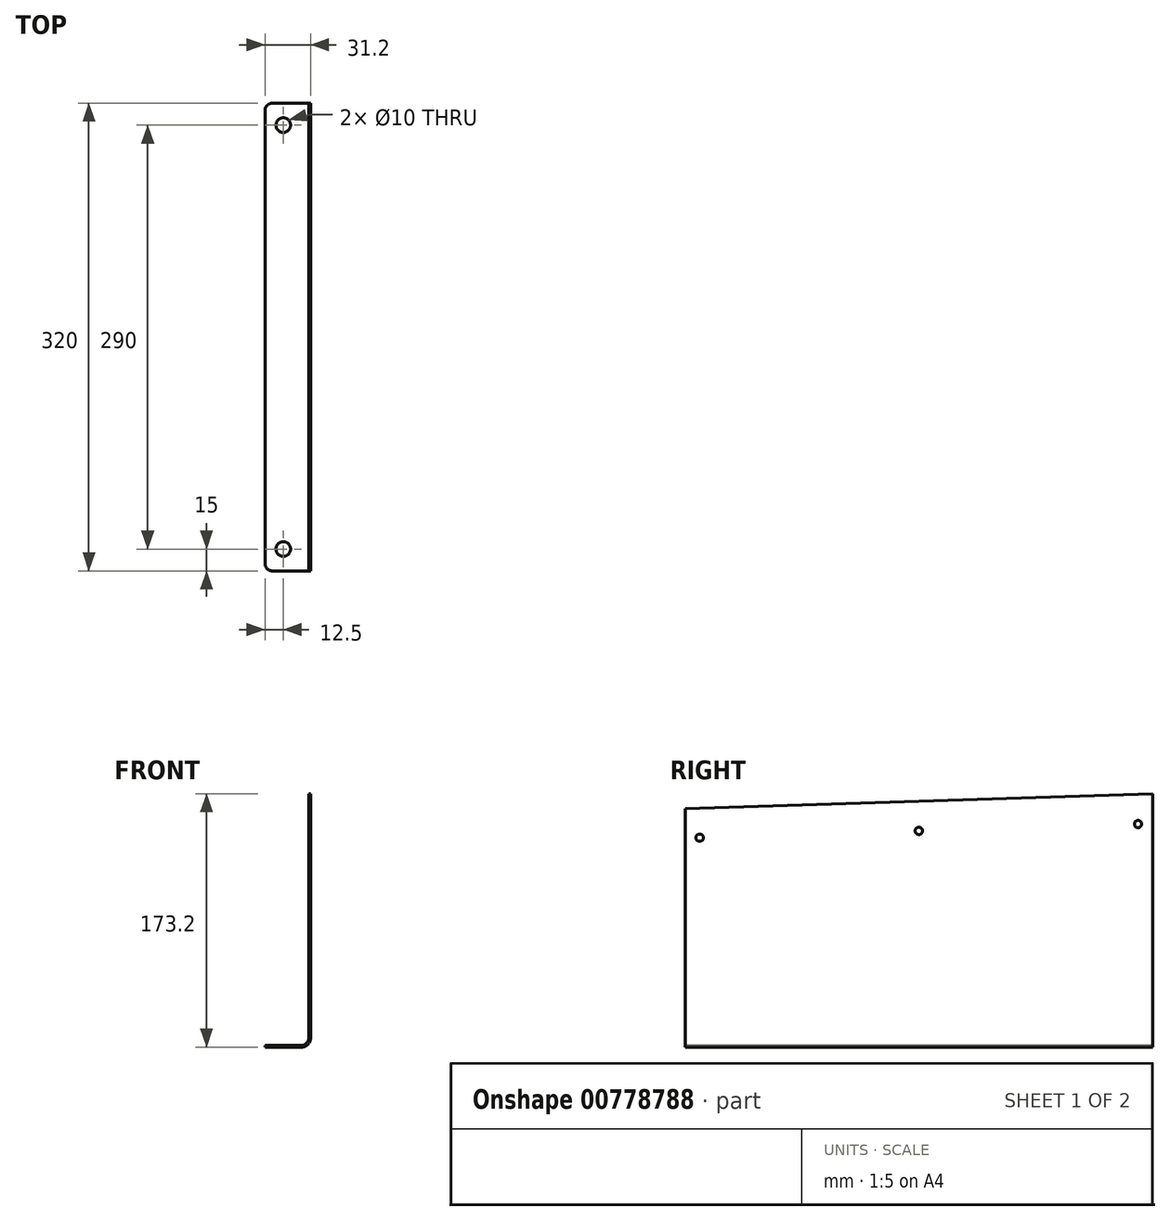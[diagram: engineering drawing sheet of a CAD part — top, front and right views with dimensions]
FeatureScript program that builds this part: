
annotation { "Feature Type Name" : "Feature", "Feature Type Description" : "" }
export const myFeature = defineFeature(function(context is Context, id is Id, definition is map)
    precondition{}
    {
        {
            var Q0;
            Q0=qCreatedBy(makeId("Front.planeOp"),FACE);
            var sketch = newSketch(context, id + "F0", { "sketchPlane" : qUnion([Q0])});
            skLineSegment(sketch, "E0", {"start": v(0, 0) * mm, "end": v(0, -167) * mm});
            skLineSegment(sketch, "E1", {"start": v(-5, -172) * mm, "end": v(-30, -172) * mm});
            skLineSegment(sketch, "E2", {"start": v(-30, -172) * mm, "end": v(-30, -173.2) * mm});
            skLineSegment(sketch, "E3", {"start": v(-30, -173.2) * mm, "end": v(-5, -173.2) * mm});
            skLineSegment(sketch, "E4", {"start": v(1.2, -167) * mm, "end": v(1.2, 0) * mm});
            skLineSegment(sketch, "E5", {"start": v(1.2, 0) * mm, "end": v(0, 0) * mm});
            skPoint(sketch, "E6.visualSharp", {"position": v(0, -172) * mm});
            skArc(sketch, "E6.filletArc", {"start": v(-5, -172) * mm, "mid": v(-1.46, -170.54) * mm, "end": v(0, -167) * mm});
            skPoint(sketch, "E7.visualSharp", {"position": v(1.2, -173.2) * mm});
            skArc(sketch, "E7.filletArc", {"start": v(-5, -173.2) * mm, "mid": v(-0.62, -171.38) * mm, "end": v(1.2, -167) * mm});
            skSolve(sketch);
        }
        {
            var Q0;
            Q0=qSketchRegion(id+"F0",true);
            extrude(context, id + "F1", {"entities" : qUnion([Q0]), "oppositeDirection" : true, "depth" : 320 * mm, "offsetDistance" : 25 * mm});
        }
        {
            var Q0;
            Q0=makeQuery(id+"F1.opExtrude","SWEPT_FACE",FACE,{"disambiguationData":[OSD([sQuery(id+"F0.wireOp",EDGE,"E1")])]});
            var sketch = newSketch(context, id + "F2", { "sketchPlane" : qUnion([Q0])});
            skCircle(sketch, "E8", {"center": v(-17.5, 305) * mm, "radius": 5 * mm});
            skCircle(sketch, "E9.0.1.0", {"center": v(-17.5, 15) * mm, "radius": 5 * mm});
            skLineSegment(sketch, "E9.direction1", {"start": v(-17.5, 305) * mm, "end": v(7.5, 305) * mm, "construction": true});
            skLineSegment(sketch, "E9.direction2", {"start": v(-17.5, 305) * mm, "end": v(-17.5, 15) * mm, "construction": true});
            skSolve(sketch);
        }
        {
            var Q0;
            Q0=qSketchRegion(id+"F2",true);
            extrude(context, id + "F3", {"entities" : qUnion([Q0]), "operationType" : NewBodyOperationType.REMOVE, "endBound" : BoundingType.UP_TO_NEXT, "oppositeDirection" : true, "depth" : 25 * mm, "offsetDistance" : 25 * mm});
        }
        {
            var Q0;
            Q0=makeQuery(id+"F1.opExtrude","CAP_EDGE",EDGE,{"disambiguationData":[OSD([sQuery(id+"F0.wireOp",EDGE,"E2")])],"isStart":false});
            var Q1;
            Q1=makeQuery(id+"F1.opExtrude","CAP_EDGE",EDGE,{"disambiguationData":[OSD([sQuery(id+"F0.wireOp",EDGE,"E2")])],"isStart":true});
            fillet(context, id + "F4", {"entities" : qUnion([Q0, Q1]), "radius" : 5 * mm, "tangentPropagation" : true, "allowEdgeOverflow" : false});
        }
        {
            var Q0;
            Q0=makeQuery(id+"F1.opExtrude","SWEPT_FACE",FACE,{"disambiguationData":[OSD([sQuery(id+"F0.wireOp",EDGE,"E0")])]});
            var sketch = newSketch(context, id + "F5", { "sketchPlane" : qUnion([Q0])});
            skLineSegment(sketch, "E10.0", {"start": v(-320, 0) * mm, "end": v(0, 0) * mm});
            skLineSegment(sketch, "E11", {"start": v(0, 0) * mm, "end": v(0, -10) * mm});
            skLineSegment(sketch, "E12", {"start": v(0, -10) * mm, "end": v(-320, 0) * mm});
            skLineSegment(sketch, "E13", {"start": v(-320, 0) * mm, "end": v(-320, 0) * mm});
            skSolve(sketch);
        }
        {
            var Q0;
            Q0=qSketchRegion(id+"F5",true);
            extrude(context, id + "F6", {"entities" : qUnion([Q0]), "operationType" : NewBodyOperationType.REMOVE, "endBound" : BoundingType.UP_TO_NEXT, "oppositeDirection" : true, "depth" : 25 * mm, "offsetDistance" : 25 * mm});
        }
        {
            var Q0;
            Q0=makeQuery(id+"F1.opExtrude","SWEPT_FACE",FACE,{"disambiguationData":[OSD([sQuery(id+"F0.wireOp",EDGE,"E4")])]});
            var sketch = newSketch(context, id + "F7", { "sketchPlane" : qUnion([Q0])});
            skCircle(sketch, "E14", {"center": v(10, -30) * mm, "radius": 2.5 * mm});
            skCircle(sketch, "E15.1.0.0", {"center": v(159.93, -25.31) * mm, "radius": 2.5 * mm});
            skCircle(sketch, "E15.2.0.0", {"center": v(309.85, -20.63) * mm, "radius": 2.5 * mm});
            skLineSegment(sketch, "E15.direction1", {"start": v(10, -30) * mm, "end": v(159.93, -25.31) * mm, "construction": true});
            skSolve(sketch);
        }
        {
            var Q0;
            Q0 = qSketchRegion(id + "F7", true);
            extrude(context, id + "F8", {"entities" : qUnion([Q0]), "operationType" : NewBodyOperationType.REMOVE, "oppositeDirection" : true, "depth" : 2 * mm, "offsetDistance" : 25 * mm});
        }
    });
